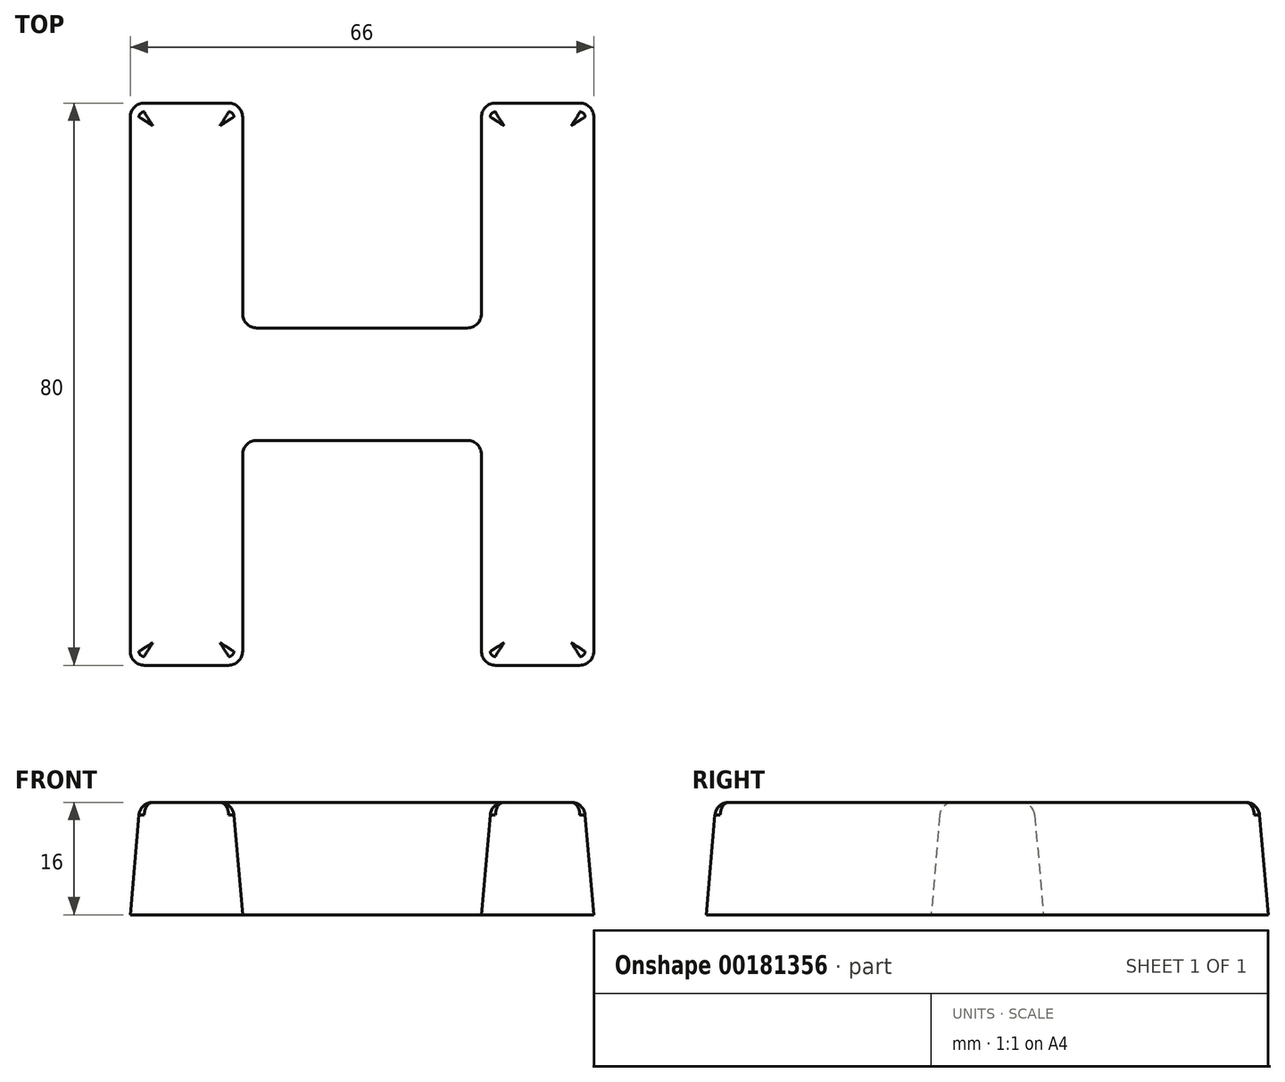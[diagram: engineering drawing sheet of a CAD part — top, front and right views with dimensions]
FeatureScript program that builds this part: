
annotation { "Feature Type Name" : "Feature", "Feature Type Description" : "" }
export const myFeature = defineFeature(function(context is Context, id is Id, definition is map)
    precondition{}
    {
        {
            var Q0;
            Q0=qCreatedBy(makeId("Top.planeOp"),FACE);
            var sketch = newSketch(context, id + "F0", { "sketchPlane" : qUnion([Q0])});
            skLineSegment(sketch, "E0.bottom", {"start": v(15, -8) * mm, "end": v(-15, -8) * mm});
            skLineSegment(sketch, "E0.top", {"start": v(15, 8) * mm, "end": v(-15, 8) * mm});
            skPoint(sketch, "E0.middle", {"position": v(0, 0) * mm});
            skLineSegment(sketch, "E1.bottom", {"start": v(31, 40) * mm, "end": v(19, 40) * mm});
            skLineSegment(sketch, "E1.top", {"start": v(31, -40) * mm, "end": v(19, -40) * mm});
            skLineSegment(sketch, "E1.left", {"start": v(33, 38) * mm, "end": v(33, -38) * mm});
            skLineSegment(sketch, "E1.right", {"start": v(17, 38) * mm, "end": v(17, 10) * mm});
            skPoint(sketch, "E1.middle", {"position": v(25, 0) * mm});
            skLineSegment(sketch, "E2.MirrorCS", {"start": v(-33, 38) * mm, "end": v(-33, -38) * mm});
            skLineSegment(sketch, "E3.MirrorCS", {"start": v(-31, 40) * mm, "end": v(-19, 40) * mm});
            skLineSegment(sketch, "E4.MirrorCS", {"start": v(-17, 38) * mm, "end": v(-17, 10) * mm});
            skLineSegment(sketch, "E5.MirrorCS", {"start": v(-31, -40) * mm, "end": v(-19, -40) * mm});
            skLineSegment(sketch, "E6.trimOffspring", {"start": v(-17, -10) * mm, "end": v(-17, -38) * mm});
            skLineSegment(sketch, "E7.trimOffspring", {"start": v(17, -10) * mm, "end": v(17, -38) * mm});
            skPoint(sketch, "E8.visualSharp", {"position": v(-33, 40) * mm});
            skArc(sketch, "E8.filletArc", {"start": v(-31, 40) * mm, "mid": v(-32.41, 39.41) * mm, "end": v(-33, 38) * mm});
            skPoint(sketch, "E9.visualSharp", {"position": v(-17, 40) * mm});
            skArc(sketch, "E9.filletArc", {"start": v(-17, 38) * mm, "mid": v(-17.59, 39.41) * mm, "end": v(-19, 40) * mm});
            skPoint(sketch, "E10.visualSharp", {"position": v(-17, 8) * mm});
            skArc(sketch, "E10.filletArc", {"start": v(-17, 10) * mm, "mid": v(-16.41, 8.59) * mm, "end": v(-15, 8) * mm});
            skPoint(sketch, "E11.visualSharp", {"position": v(17, 8) * mm});
            skArc(sketch, "E11.filletArc", {"start": v(15, 8) * mm, "mid": v(16.41, 8.59) * mm, "end": v(17, 10) * mm});
            skPoint(sketch, "E12.visualSharp", {"position": v(17, 40) * mm});
            skArc(sketch, "E12.filletArc", {"start": v(19, 40) * mm, "mid": v(17.59, 39.41) * mm, "end": v(17, 38) * mm});
            skPoint(sketch, "E13.visualSharp", {"position": v(33, 40) * mm});
            skArc(sketch, "E13.filletArc", {"start": v(33, 38) * mm, "mid": v(32.41, 39.41) * mm, "end": v(31, 40) * mm});
            skPoint(sketch, "E14.visualSharp", {"position": v(33, -40) * mm});
            skArc(sketch, "E14.filletArc", {"start": v(31, -40) * mm, "mid": v(32.41, -39.41) * mm, "end": v(33, -38) * mm});
            skPoint(sketch, "E15.visualSharp", {"position": v(17, -40) * mm});
            skArc(sketch, "E15.filletArc", {"start": v(17, -38) * mm, "mid": v(17.59, -39.41) * mm, "end": v(19, -40) * mm});
            skPoint(sketch, "E16.visualSharp", {"position": v(-17, -40) * mm});
            skArc(sketch, "E16.filletArc", {"start": v(-19, -40) * mm, "mid": v(-17.59, -39.41) * mm, "end": v(-17, -38) * mm});
            skPoint(sketch, "E17.visualSharp", {"position": v(-17, -8) * mm});
            skArc(sketch, "E17.filletArc", {"start": v(-15, -8) * mm, "mid": v(-16.41, -8.59) * mm, "end": v(-17, -10) * mm});
            skPoint(sketch, "E18.visualSharp", {"position": v(17, -8) * mm});
            skArc(sketch, "E18.filletArc", {"start": v(17, -10) * mm, "mid": v(16.41, -8.59) * mm, "end": v(15, -8) * mm});
            skPoint(sketch, "E19.visualSharp", {"position": v(-33, -40) * mm});
            skArc(sketch, "E19.filletArc", {"start": v(-33, -38) * mm, "mid": v(-32.41, -39.41) * mm, "end": v(-31, -40) * mm});
            skSolve(sketch);
        }
        {
            var Q0;
            Q0 = qSketchRegion(id + "F0", true);
            extrude(context, id + "F1", {"entities" : qUnion([Q0]), "depth" : 16 * mm, "hasDraft" : true, "draftAngle" : 5 * degree, "draftPullDirection" : true});
        }
        {
            var Q0;
            Q0=makeQuery(id+"F1.opExtrude","CAP_FACE",FACE,{"disambiguationData":[OSD([sQuery(id+"F0.wireOp",EDGE,"E0.bottom"),sQuery(id+"F0.wireOp",EDGE,"E0.top"),sQuery(id+"F0.wireOp",EDGE,"E1.bottom"),sQuery(id+"F0.wireOp",EDGE,"E1.top"),sQuery(id+"F0.wireOp",EDGE,"E1.left"),sQuery(id+"F0.wireOp",EDGE,"E1.right"),sQuery(id+"F0.wireOp",EDGE,"E2.MirrorCS"),sQuery(id+"F0.wireOp",EDGE,"E3.MirrorCS"),sQuery(id+"F0.wireOp",EDGE,"E4.MirrorCS"),sQuery(id+"F0.wireOp",EDGE,"E5.MirrorCS"),sQuery(id+"F0.wireOp",EDGE,"E6.trimOffspring"),sQuery(id+"F0.wireOp",EDGE,"E7.trimOffspring"),sQuery(id+"F0.wireOp",EDGE,"E8.filletArc"),sQuery(id+"F0.wireOp",EDGE,"E9.filletArc"),sQuery(id+"F0.wireOp",EDGE,"E10.filletArc"),sQuery(id+"F0.wireOp",EDGE,"E11.filletArc"),sQuery(id+"F0.wireOp",EDGE,"E12.filletArc"),sQuery(id+"F0.wireOp",EDGE,"E13.filletArc"),sQuery(id+"F0.wireOp",EDGE,"E14.filletArc"),sQuery(id+"F0.wireOp",EDGE,"E15.filletArc"),sQuery(id+"F0.wireOp",EDGE,"E16.filletArc"),sQuery(id+"F0.wireOp",EDGE,"E17.filletArc"),sQuery(id+"F0.wireOp",EDGE,"E18.filletArc"),sQuery(id+"F0.wireOp",EDGE,"E19.filletArc")])],"isStart":false});
            fillet(context, id + "F2", {"entities" : qUnion([Q0]), "radius" : 2 * mm, "tangentPropagation" : true, "allowEdgeOverflow" : false});
        }
    });
